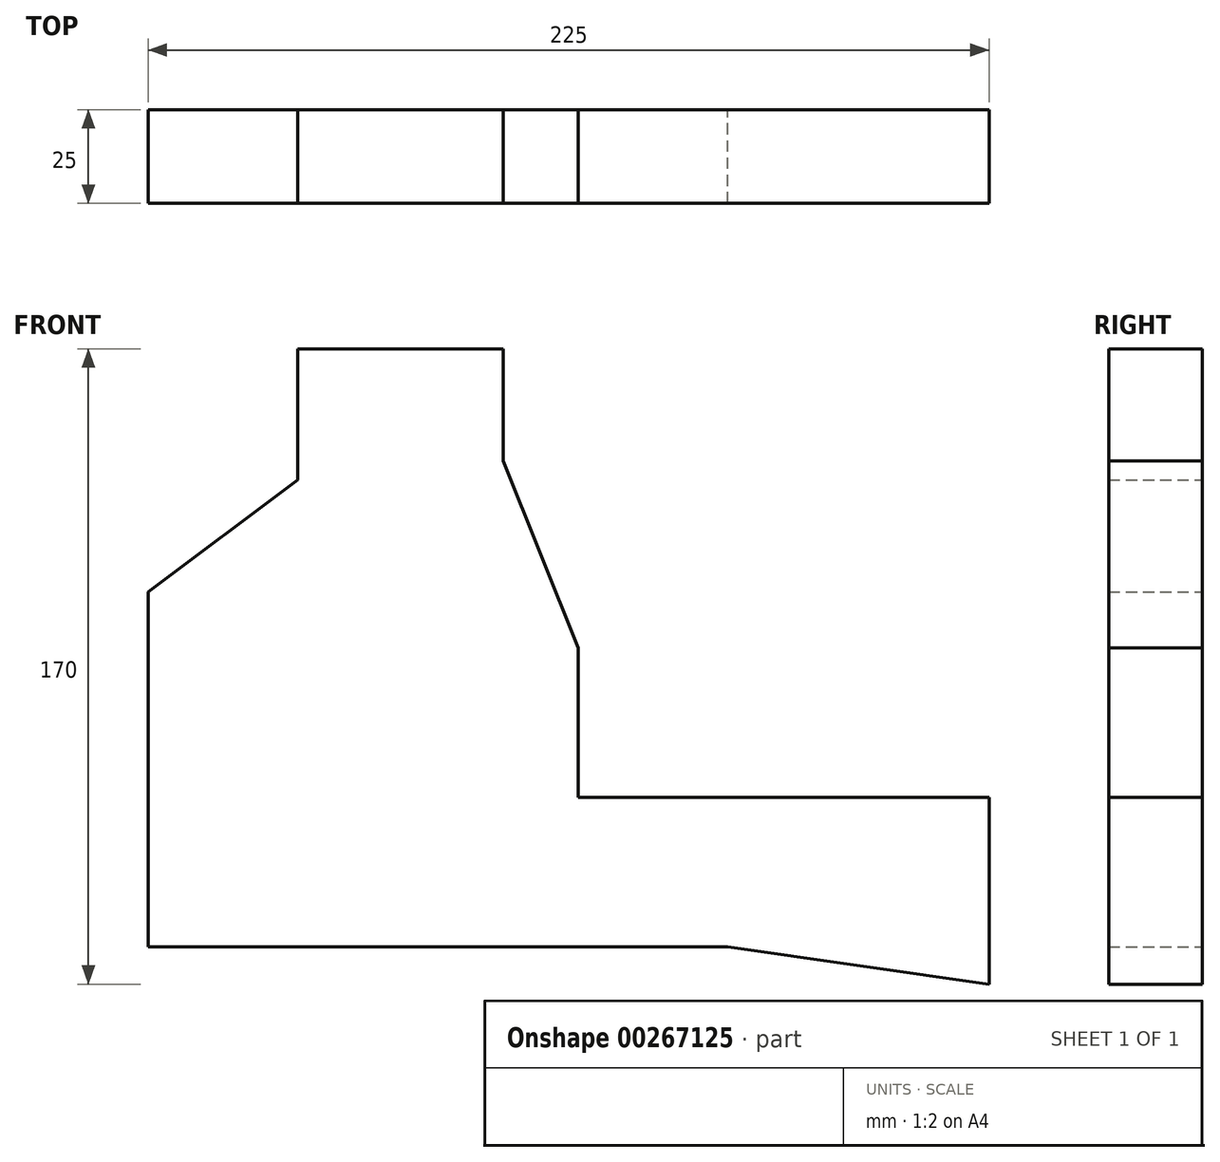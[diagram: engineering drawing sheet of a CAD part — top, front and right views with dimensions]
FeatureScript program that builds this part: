
annotation { "Feature Type Name" : "Feature", "Feature Type Description" : "" }
export const myFeature = defineFeature(function(context is Context, id is Id, definition is map)
    precondition{}
    {
        {
            var Q0;
            Q0=qCreatedBy(makeId("Front.planeOp"),FACE);
            var sketch = newSketch(context, id + "F0", { "sketchPlane" : qUnion([Q0])});
            skLineSegment(sketch, "E0", {"start": v(-47.33, -46.4) * mm, "end": v(-47.33, 48.6) * mm});
            skLineSegment(sketch, "E1", {"start": v(-7.33, 78.6) * mm, "end": v(-47.33, 48.6) * mm});
            skLineSegment(sketch, "E2", {"start": v(-7.33, 78.6) * mm, "end": v(-7.33, 113.6) * mm});
            skLineSegment(sketch, "E3", {"start": v(-7.33, 113.6) * mm, "end": v(47.67, 113.6) * mm});
            skLineSegment(sketch, "E4", {"start": v(47.67, 113.6) * mm, "end": v(47.67, 83.6) * mm});
            skLineSegment(sketch, "E5", {"start": v(67.67, 33.6) * mm, "end": v(47.67, 83.6) * mm});
            skLineSegment(sketch, "E6", {"start": v(67.67, 33.6) * mm, "end": v(67.67, -6.4) * mm});
            skLineSegment(sketch, "E7", {"start": v(67.67, -6.4) * mm, "end": v(177.67, -6.4) * mm});
            skLineSegment(sketch, "E8", {"start": v(177.67, -6.4) * mm, "end": v(177.67, -56.4) * mm});
            skLineSegment(sketch, "E9", {"start": v(-47.33, -46.4) * mm, "end": v(107.67, -46.4) * mm});
            skLineSegment(sketch, "E10", {"start": v(107.67, -46.4) * mm, "end": v(177.67, -56.4) * mm});
            skSolve(sketch);
        }
        {
            var Q0;
            Q0=makeQuery(id+"F0.imprint","IMPRINT",FACE,{"disambiguationData":[TD([[makeQuery(id+"F0.imprint","IMPRINT",EDGE,{"derivedFrom":sQuery(id+"F0.wireOp",EDGE,"E0")}),-1.0]])]});
            extrude(context, id + "F1", {"entities" : qUnion([Q0]), "depth" : 25 * mm});
        }
    });
